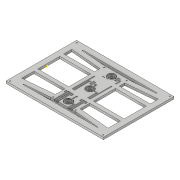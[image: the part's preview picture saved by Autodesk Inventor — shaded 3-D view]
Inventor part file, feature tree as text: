
AUTODESK INVENTOR PART (.ipt)
format: ipt  version: 2022 (Build 260153000, 153)  size: 577,024 bytes
history: native  units: mm
features: sketch x10, extrude x9, fillet x1
ambient origin geometry x8: Origin, YZ Plane, XZ Plane, XY Plane, X Axis, Y Axis, Z Axis, Center Point
bodies: Solid1 (feature_tree)
feature tree (20):
  extrude  "Extrusion1"  Depth=3.7mm
  fillet  "Fillet1"  Radius=3.7mm
  extrude  "Extrusion2"  Depth=39.2mm
  extrude  "Extrusion3"  Depth=45.0mm
  extrude  "Extrusion4"  Depth=5.0mm
  extrude  "Extrusion6"  Depth=10.0mm
  extrude  "Extrusion7"  Depth=8.5mm
  extrude  "Extrusion8"  Depth=2.0mm
  extrude  "Extrusion9"  Depth=4.0mm TaperAngle=0.0deg
  sketch  "Sketch10"  dims[d18=0.5mm d19=5.8mm]
  extrude  "Extrusion10"  Depth=0.5mm
  sketch  "Sketch1"  dims[d0=0.0mm d1=3.7mm d2=3.7mm]
  sketch  "Sketch2"  dims[d3=3.7mm d4=39.2mm]
  sketch  "Sketch3"  dims[d5=39.2mm d6=45.0mm]
  sketch  "Sketch4"  dims[d7=98.4mm d8=5.0mm]
  sketch  "Sketch6"  dims[d9=56.1mm d10=10.0mm]
  sketch  "Sketch7"  dims[d11=10.0mm d12=8.5mm]
  sketch  "Sketch8"  dims[d13=2.0mm d14=2.0mm]
  sketch  "Sketch9"  dims[d15=3.0mm d16=4.0mm d17=0.0mm]
  sketch  "Sketch11"  dims[d20=5.8mm d21=5.8mm d22=1.6mm d23=0.0mm d24=4.0mm d25=3.5mm d26=2.0mm d27=1.6mm d28=0.0mm d29=4.1mm d30=2.5mm d31=0.0mm d64=8.0mm d65=10.0mm d68=22.5deg d69=22.5deg d70=6.0mm d71=7.0mm d72=20.0mm d74=39.2mm d75=10.0mm d77=10.0mm d79=2.0mm d80=0.0mm d81=0.75mm d82=1.5mm d83=0.1mm d85=15.0mm d86=11.0mm d87=1.5mm d88=0.1mm d89=1.5mm d91=8.0mm d93=14.0mm d94=1.5mm d95=1.5mm d96=1.5mm d97=0.75mm d98=0.1mm d99=0.75mm d100=1.5mm d101=8.0mm d102=17.0mm d103=1.5mm d105=1.5mm d106=0.1mm d107=0.75mm d108=1.5mm d109=4.5mm d110=1.5mm d111=0.1mm d112=0.75mm d113=1.5mm d114=7.5mm d115=1.5mm d116=0.1mm d117=0.75mm d118=1.5mm d119=10.5mm d120=1.5mm d121=2.0mm d122=0.0mm d123=1.0mm d124=1.0mm d125=10.0mm d126=0.75mm d127=0.75mm d128=12.0mm d129=10.0mm d131=10.0mm d132=20.0mm d134=3.0mm d136=10.0mm d138=10.0mm d139=20.0mm d141=6.0mm d143=1.0mm d144=4.5mm d145=1.0mm d146=1.0mm d147=1.0mm d148=4.5mm d149=1.0mm d150=1.0mm d151=1.0mm d152=1.0mm d153=1.0mm d154=4.5mm d155=1.5mm d156=0.0mm d157=4.0mm d158=1.5mm d159=2.5mm d160=1.5mm d161=1.5mm d162=1.5mm d163=2.5mm d164=4.0mm d165=4.0mm d166=1.5mm d167=1.5mm d168=1.5mm d169=1.5mm d170=3.5mm d171=1.5mm d172=1.5mm d173=1.5mm d174=1.5mm d175=1.5mm d176=4.0mm d177=1.5mm d178=1.5mm d179=1.5mm d180=2.5mm d181=1.5mm d182=1.5mm d183=4.0mm d184=1.5mm d185=2.5mm d186=1.5mm d187=1.5mm d188=0.0mm d189=10.0mm d190=0.0mm]
